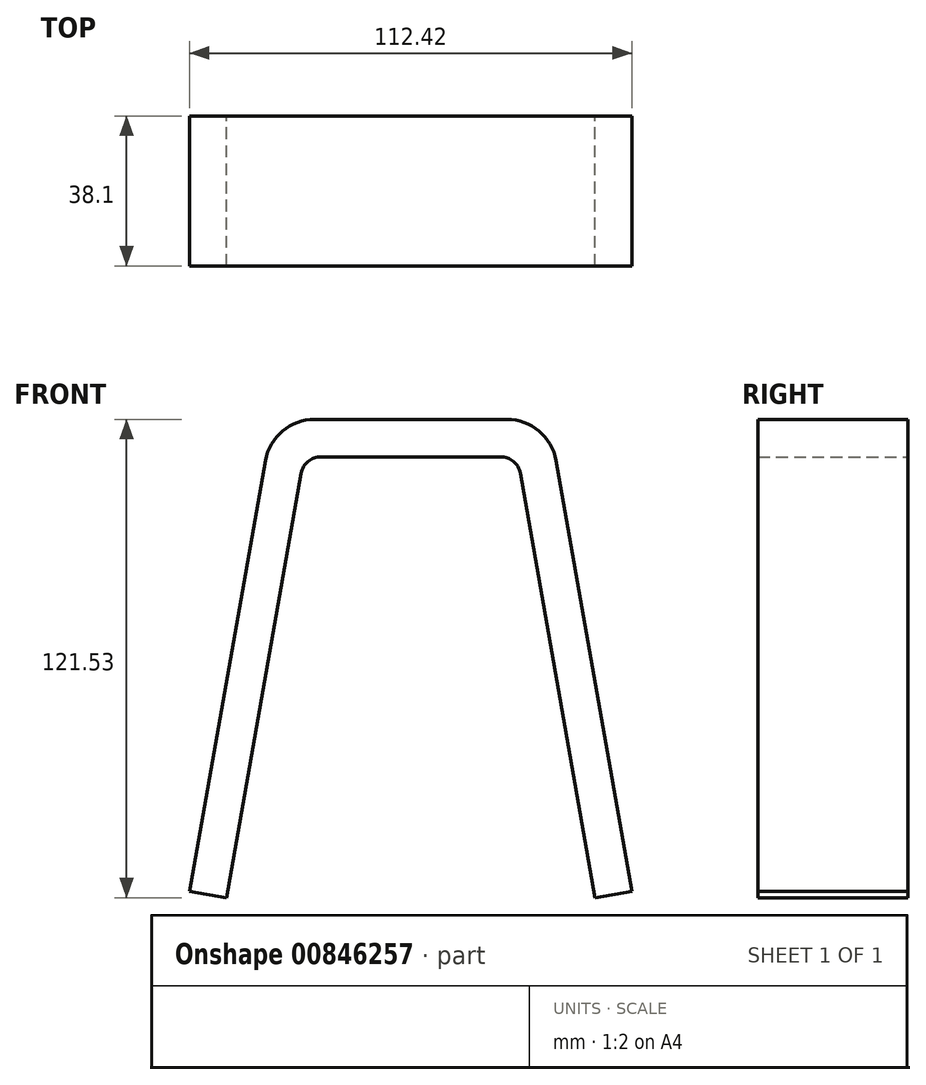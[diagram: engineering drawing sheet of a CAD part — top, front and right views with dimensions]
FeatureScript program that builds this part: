
annotation { "Feature Type Name" : "Feature", "Feature Type Description" : "" }
export const myFeature = defineFeature(function(context is Context, id is Id, definition is map)
    precondition{}
    {
        {
            var Q0;
            Q0=qCreatedBy(makeId("Front.planeOp"),FACE);
            var sketch = newSketch(context, id + "F0", { "sketchPlane" : qUnion([Q0])});
            skLineSegment(sketch, "E0.top", {"start": v(35.07, 41.77) * mm, "end": v(-35.07, 41.77) * mm});
            skPoint(sketch, "E0.middle", {"position": v(0, 2.09) * mm});
            skLineSegment(sketch, "E1", {"start": v(-27.08, 32.25) * mm, "end": v(-37.72, -28.08) * mm});
            skLineSegment(sketch, "E2.MirrorCS", {"start": v(27.08, 32.25) * mm, "end": v(37.72, -28.08) * mm});
            skLineSegment(sketch, "E3.0", {"start": v(27.08, 32.25) * mm, "end": v(-27.08, 32.25) * mm});
            skLineSegment(sketch, "E4.0", {"start": v(-34.79, 43.4) * mm, "end": v(-47.39, -28.08) * mm});
            skLineSegment(sketch, "E5.0", {"start": v(34.78, 43.43) * mm, "end": v(47.39, -28.08) * mm});
            skLineSegment(sketch, "E6", {"start": v(-37.72, -28.08) * mm, "end": v(-39.4, -37.6) * mm});
            skLineSegment(sketch, "E7", {"start": v(37.72, -28.08) * mm, "end": v(39.4, -37.6) * mm});
            skPoint(sketch, "E8.trimOffspring.end.orphan", {"position": v(96.84, 41.77) * mm});
            skPoint(sketch, "E9.orphan", {"position": v(25.4, 41.77) * mm});
            skPoint(sketch, "E10.orphan", {"position": v(-25.4, 41.77) * mm});
            skPoint(sketch, "E11.orphan", {"position": v(-96.84, 41.77) * mm});
            skLineSegment(sketch, "E12", {"start": v(-47.39, -28.08) * mm, "end": v(-56.2, -78.1) * mm});
            skLineSegment(sketch, "E13", {"start": v(-37.72, -28.08) * mm, "end": v(-46.54, -78.1) * mm});
            skLineSegment(sketch, "E14", {"start": v(-56.2, -78.1) * mm, "end": v(-46.83, -79.76) * mm});
            skLineSegment(sketch, "E15", {"start": v(-46.54, -78.1) * mm, "end": v(-46.83, -79.76) * mm});
            skLineSegment(sketch, "E16.MirrorCS", {"start": v(37.72, -28.08) * mm, "end": v(46.54, -78.1) * mm});
            skLineSegment(sketch, "E17.MirrorCS", {"start": v(47.39, -28.08) * mm, "end": v(56.2, -78.1) * mm});
            skLineSegment(sketch, "E18.MirrorCS", {"start": v(56.2, -78.1) * mm, "end": v(46.83, -79.76) * mm});
            skPoint(sketch, "E0.right.end.orphan", {"position": v(-96.84, -28.08) * mm});
            skPoint(sketch, "E0.right.start.orphan", {"position": v(-96.84, -37.6) * mm});
            skPoint(sketch, "E0.left.start.orphan", {"position": v(96.84, -37.6) * mm});
            skLineSegment(sketch, "E19.MirrorCS", {"start": v(46.54, -78.1) * mm, "end": v(46.83, -79.76) * mm});
            skSolve(sketch);
        }
        {
            var Q0;
            Q0 = qSketchRegion(id + "F0", true);
            extrude(context, id + "F1", {"entities" : qUnion([Q0]), "depth" : 38.1 * mm, "offsetDistance" : 25.4 * mm});
        }
        {
            var Q0;
            Q0=makeQuery(id+"F1.opExtrude","SWEPT_EDGE",EDGE,{"disambiguationData":[OSD([sQuery(id+"F0.wireOp",EDGE,"E1"),sQuery(id+"F0.wireOp",EDGE,"E3.0")])]});
            var Q1;
            Q1=makeQuery(id+"F1.opExtrude","SWEPT_EDGE",EDGE,{"disambiguationData":[OSD([sQuery(id+"F0.wireOp",EDGE,"E2.MirrorCS"),sQuery(id+"F0.wireOp",EDGE,"E3.0")])]});
            fillet(context, id + "F2", {"entities" : qUnion([Q0, Q1]), "radius" : 5.08 * mm, "tangentPropagation" : true, "allowEdgeOverflow" : false});
        }
        {
            var Q0;
            Q0=makeQuery(id+"F1.opExtrude","SWEPT_EDGE",EDGE,{"disambiguationData":[OSD([sQuery(id+"F0.wireOp",EDGE,"E0.top"),sQuery(id+"F0.wireOp",EDGE,"E4.0")])]});
            var Q1;
            Q1=makeQuery(id+"F1.opExtrude","SWEPT_EDGE",EDGE,{"disambiguationData":[OSD([sQuery(id+"F0.wireOp",EDGE,"E0.top"),sQuery(id+"F0.wireOp",EDGE,"E5.0")])]});
            fillet(context, id + "F3", {"entities" : qUnion([Q0, Q1]), "radius" : 12.7 * mm, "tangentPropagation" : true, "allowEdgeOverflow" : false});
        }
    });
